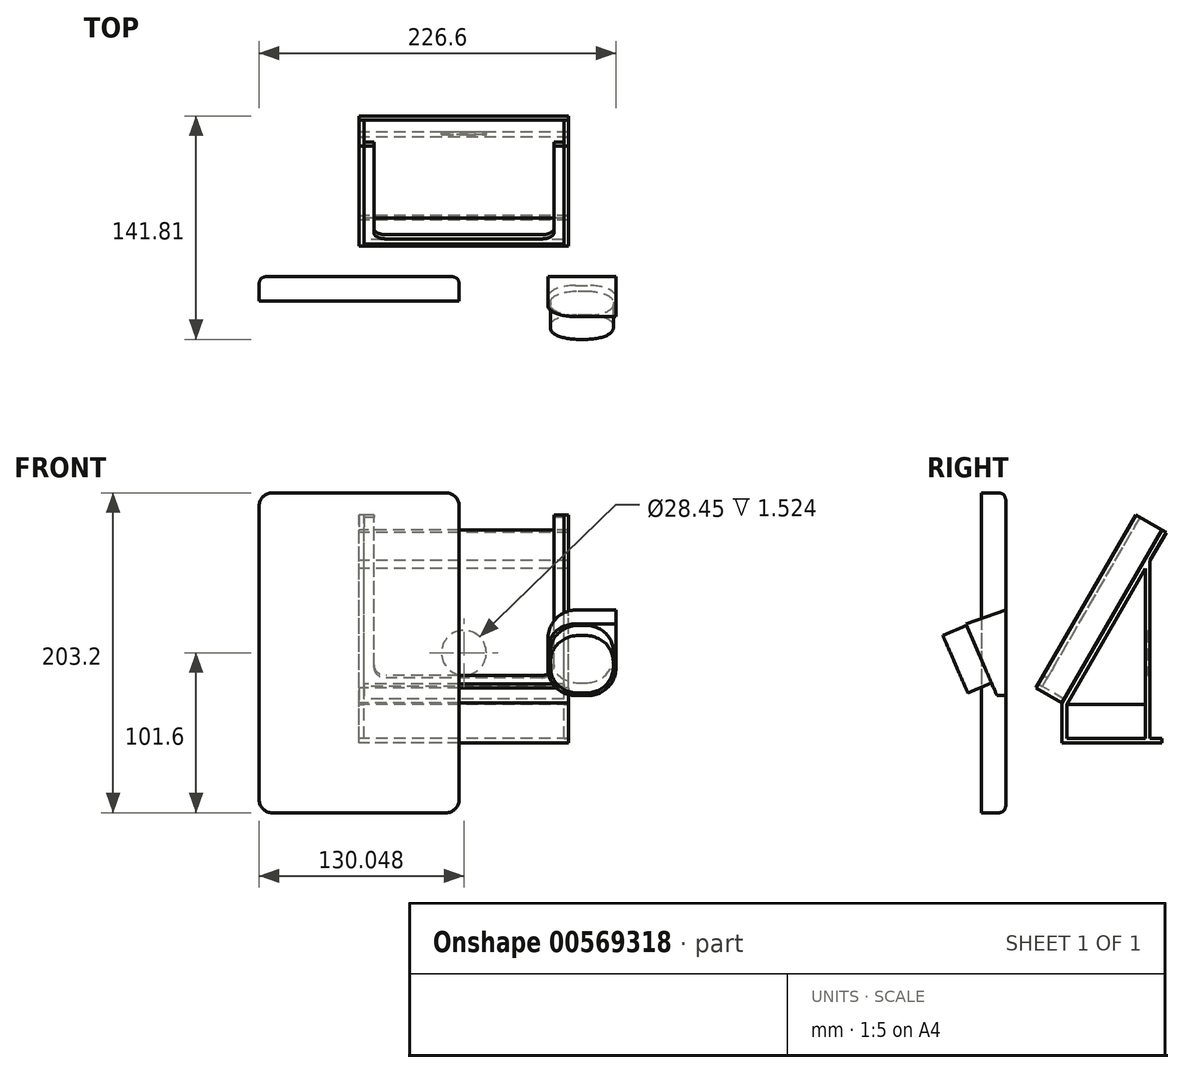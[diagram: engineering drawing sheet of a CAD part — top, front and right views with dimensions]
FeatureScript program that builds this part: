
annotation { "Feature Type Name" : "Feature", "Feature Type Description" : "" }
export const myFeature = defineFeature(function(context is Context, id is Id, definition is map)
    precondition{}
    {
        {
            var Q0;
            Q0=qCreatedBy(makeId("Front.planeOp"),FACE);
            var sketch = newSketch(context, id + "F0", { "sketchPlane" : qUnion([Q0])});
            skLineSegment(sketch, "E0.bottom", {"start": v(63.5, 101.6) * mm, "end": v(-63.5, 101.6) * mm});
            skLineSegment(sketch, "E0.top", {"start": v(63.5, -101.6) * mm, "end": v(-63.5, -101.6) * mm});
            skLineSegment(sketch, "E0.left", {"start": v(63.5, 101.6) * mm, "end": v(63.5, -101.6) * mm});
            skLineSegment(sketch, "E0.right", {"start": v(-63.5, 101.6) * mm, "end": v(-63.5, -101.6) * mm});
            skPoint(sketch, "E0.middle", {"position": v(0, 0) * mm});
            skSolve(sketch);
        }
        {
            var Q0;
            Q0=makeQuery(id+"F0.imprint","IMPRINT",FACE,{"disambiguationData":[TD([[makeQuery(id+"F0.imprint","IMPRINT",EDGE,{"derivedFrom":sQuery(id+"F0.wireOp",EDGE,"E0.bottom")}),1.0]])]});
            extrude(context, id + "F1", {"entities" : qUnion([Q0]), "depth" : 15.44 * mm, "offsetDistance" : 25.4 * mm});
        }
        {
            var Q0;
            Q0=makeQuery(id+"F1.opExtrude","SWEPT_EDGE",EDGE,{"disambiguationData":[OSD([sQuery(id+"F0.wireOp",EDGE,"E0.top"),sQuery(id+"F0.wireOp",EDGE,"E0.right")])]});
            var Q1;
            Q1=makeQuery(id+"F1.opExtrude","SWEPT_EDGE",EDGE,{"disambiguationData":[OSD([sQuery(id+"F0.wireOp",EDGE,"E0.top"),sQuery(id+"F0.wireOp",EDGE,"E0.left")])]});
            var Q2;
            Q2=makeQuery(id+"F1.opExtrude","SWEPT_EDGE",EDGE,{"disambiguationData":[OSD([sQuery(id+"F0.wireOp",EDGE,"E0.bottom"),sQuery(id+"F0.wireOp",EDGE,"E0.left")])]});
            var Q3;
            Q3=makeQuery(id+"F1.opExtrude","SWEPT_EDGE",EDGE,{"disambiguationData":[OSD([sQuery(id+"F0.wireOp",EDGE,"E0.bottom"),sQuery(id+"F0.wireOp",EDGE,"E0.right")])]});
            fillet(context, id + "F2", {"entities" : qUnion([Q0, Q1, Q2, Q3]), "radius" : 8.38 * mm, "tangentPropagation" : true, "allowEdgeOverflow" : false});
        }
        {
            var Q0;
            Q0=makeQuery(id+"F1.opExtrude","CAP_FACE",FACE,{"disambiguationData":[OSD([sQuery(id+"F0.wireOp",EDGE,"E0.bottom"),sQuery(id+"F0.wireOp",EDGE,"E0.top"),sQuery(id+"F0.wireOp",EDGE,"E0.left"),sQuery(id+"F0.wireOp",EDGE,"E0.right")])],"isStart":true});
            fillet(context, id + "F3", {"entities" : qUnion([Q0]), "radius" : 5.08 * mm, "tangentPropagation" : true, "rho" : .5, "crossSection" : FilletCrossSection.CONIC, "allowEdgeOverflow" : false});
        }
        {
            var Q0;
            Q0=qCreatedBy(makeId("Front.planeOp"),FACE);
            var sketch = newSketch(context, id + "F4", { "sketchPlane" : qUnion([Q0])});
            skLineSegment(sketch, "E1.bottom", {"start": v(163.1, 27.18) * mm, "end": v(119.92, 27.18) * mm});
            skLineSegment(sketch, "E1.top", {"start": v(163.1, -27.18) * mm, "end": v(119.92, -27.18) * mm});
            skLineSegment(sketch, "E1.left", {"start": v(163.1, 27.18) * mm, "end": v(163.1, -27.18) * mm});
            skLineSegment(sketch, "E1.right", {"start": v(119.92, 27.18) * mm, "end": v(119.92, -27.18) * mm});
            skPoint(sketch, "E1.middle", {"position": v(141.51, 0) * mm});
            skPoint(sketch, "E2.visualSharp", {"position": v(119.92, 27.18) * mm});
            skPoint(sketch, "E3.visualSharp", {"position": v(163.1, 27.18) * mm});
            skPoint(sketch, "E4.visualSharp", {"position": v(119.92, -27.18) * mm});
            skPoint(sketch, "E5.visualSharp", {"position": v(163.1, -27.18) * mm});
            skSolve(sketch);
        }
        {
            var Q0;
            Q0=makeQuery(id+"F4.imprint","IMPRINT",FACE,{"disambiguationData":[TD([[makeQuery(id+"F4.imprint","IMPRINT",EDGE,{"derivedFrom":sQuery(id+"F4.wireOp",EDGE,"E1.bottom")}),1.0]])]});
            extrude(context, id + "F5", {"entities" : qUnion([Q0]), "depth" : 25.4 * mm, "offsetDistance" : 25.4 * mm});
        }
        {
            var Q0;
            Q0=makeQuery(id+"F5.opExtrude","SWEPT_FACE",FACE,{"disambiguationData":[OSD([sQuery(id+"F4.wireOp",EDGE,"E1.left")])]});
            var sketch = newSketch(context, id + "F6", { "sketchPlane" : qUnion([Q0])});
            skLineSegment(sketch, "E6.0", {"start": v(-25.4, 27.18) * mm, "end": v(0, 27.18) * mm});
            skLineSegment(sketch, "E7", {"start": v(-5.56, -27.18) * mm, "end": v(-25.4, 18.47) * mm});
            skLineSegment(sketch, "E8", {"start": v(0, 27.18) * mm, "end": v(-25.4, 18.47) * mm});
            skLineSegment(sketch, "E9", {"start": v(-5.56, -27.18) * mm, "end": v(-25.4, -27.18) * mm});
            skLineSegment(sketch, "E10", {"start": v(-25.4, -27.18) * mm, "end": v(-25.4, 18.47) * mm});
            skLineSegment(sketch, "E11", {"start": v(-25.4, 18.47) * mm, "end": v(-25.4, 27.18) * mm});
            skSolve(sketch);
        }
        {
            var Q0;
            {var subQ0=sQuery(id+"F6.wireOp",EDGE,"E9");Q0=makeQuery(id+"F6.imprint","IMPRINT",FACE,{"disambiguationData":[TD([[makeQuery(id+"F6.imprint","IMPRINT",EDGE,{"derivedFrom":subQ0}),-1.0]])]});}
            var Q1;
            {var subQ0=sQuery(id+"F6.wireOp",EDGE,"E7");var subQ1=sQuery(id+"F4.wireOp",EDGE,"E1.left");var subQ2=makeQuery(id+"F5.opExtrude","SWEPT_EDGE",EDGE,{"disambiguationData":[OSD([subQ1,sQuery(id+"F4.wireOp",EDGE,"E5.filletArc")])]});var subQ3=makeQuery(id+"F6.imprint","INTERSECT",VERTEX,{"derivedFrom":[subQ2,subQ0]});Q1=makeQuery(id+"F6.imprint","IMPRINT",FACE,{"disambiguationData":[TD([[makeQuery(id+"F6.imprint","IMPRINT",EDGE,{"disambiguationData":[TD([[subQ3,-1.0]])],"derivedFrom":subQ0}),1.0]])]});}
            var Q2;
            {var subQ1=sQuery(id+"F6.wireOp",EDGE,"E7");var subQ3=makeQuery(id+"F5.opExtrude","SWEPT_EDGE",EDGE,{"disambiguationData":[OSD([sQuery(id+"F4.wireOp",EDGE,"E1.left"),sQuery(id+"F4.wireOp",EDGE,"E3.filletArc")])]});var subQ4=makeQuery(id+"F6.imprint","INTERSECT",VERTEX,{"derivedFrom":[subQ3,subQ1]});Q2=makeQuery(id+"F6.imprint","IMPRINT",FACE,{"disambiguationData":[TD([[makeQuery(id+"F6.imprint","IMPRINT",EDGE,{"disambiguationData":[TD([[subQ4,-1.0]])],"derivedFrom":subQ1}),1.0]])]});}
            var Q3;
            Q3=makeQuery(id+"F6.imprint","IMPRINT",FACE,{"disambiguationData":[TD([[makeQuery(id+"F6.imprint","IMPRINT",EDGE,{"derivedFrom":sQuery(id+"F6.wireOp",EDGE,"E6.0")}),-1.0]])]});
            extrude(context, id + "F7", {"entities" : qUnion([Q0, Q1, Q2, Q3]), "operationType" : NewBodyOperationType.REMOVE, "oppositeDirection" : true, "depth" : 50.8 * mm, "offsetDistance" : 25.4 * mm});
        }
        {
            var Q0;
            Q0=makeQuery(id+"F5.opExtrude","SWEPT_EDGE",EDGE,{"disambiguationData":[OSD([sQuery(id+"F4.wireOp",EDGE,"E1.top"),sQuery(id+"F4.wireOp",EDGE,"E1.left")])]});
            var Q1;
            Q1=makeQuery(id+"F5.opExtrude","SWEPT_EDGE",EDGE,{"disambiguationData":[OSD([sQuery(id+"F4.wireOp",EDGE,"E1.top"),sQuery(id+"F4.wireOp",EDGE,"E1.right")])]});
            var Q2;
            Q2=makeQuery(id+"F7.boolean.opBoolean","INTERSECT",EDGE,{"derivedFrom":[makeQuery(id+"F5.opExtrude","SWEPT_FACE",FACE,{"disambiguationData":[OSD([sQuery(id+"F4.wireOp",EDGE,"E1.right")])]}),makeQuery(id+"F7.opExtrude","SWEPT_FACE",FACE,{"disambiguationData":[OSD([sQuery(id+"F6.wireOp",EDGE,"E8")])]})]});
            var Q3;
            Q3=makeQuery(id+"F7.boolean.opBoolean","COPY",EDGE,{"derivedFrom":makeQuery(id+"F7.opExtrude","CAP_EDGE",EDGE,{"disambiguationData":[OSD([sQuery(id+"F6.wireOp",EDGE,"E8")])],"isStart":true})});
            fillet(context, id + "F8", {"entities" : qUnion([Q0, Q1, Q2, Q3]), "radius" : 17.53 * mm, "tangentPropagation" : true, "allowEdgeOverflow" : false});
        }
        {
            var Q0;
            Q0=makeQuery(id+"F7.boolean.opBoolean","COPY",FACE,{"derivedFrom":makeQuery(id+"F7.opExtrude","SWEPT_FACE",FACE,{"disambiguationData":[OSD([sQuery(id+"F6.wireOp",EDGE,"E7")])]})});
            var sketch = newSketch(context, id + "F9", { "sketchPlane" : qUnion([Q0])});
            skLineSegment(sketch, "E12.0", {"start": v(121.6, 25.92) * mm, "end": v(161.41, 25.92) * mm});
            skLineSegment(sketch, "E13.0", {"start": v(121.6, -13.88) * mm, "end": v(161.41, -13.88) * mm});
            skLineSegment(sketch, "E14.0", {"start": v(161.41, -13.88) * mm, "end": v(161.41, 25.92) * mm});
            skLineSegment(sketch, "E15.0", {"start": v(121.6, -13.88) * mm, "end": v(121.6, 25.92) * mm});
            skPoint(sketch, "E16.orphan", {"position": v(137.45, 25.92) * mm});
            skPoint(sketch, "E17.orphan", {"position": v(145.57, 25.92) * mm});
            skPoint(sketch, "E18.orphan", {"position": v(137.45, -13.88) * mm});
            skPoint(sketch, "E19.orphan", {"position": v(145.57, -13.88) * mm});
            skSolve(sketch);
        }
        {
            var Q0;
            {var subQ1=makeQuery(id+"F7.boolean.opBoolean","COPY",FACE,{"derivedFrom":makeQuery(id+"F7.opExtrude","SWEPT_FACE",FACE,{"disambiguationData":[OSD([sQuery(id+"F6.wireOp",EDGE,"E7")])]})});var subQ6=sQuery(id+"F6.wireOp",EDGE,"E8");var subQ14=makeQuery(id+"F8.opFillet","BLEND_EDGE",EDGE,{"blendedFrom":[makeQuery(id+"F7.boolean.opBoolean","COPY",EDGE,{"derivedFrom":makeQuery(id+"F7.opExtrude","CAP_EDGE",EDGE,{"disambiguationData":[OSD([subQ6])],"isStart":true})}),subQ1],"blendedInto":[subQ1]});var subQ16=sQuery(id+"F9.wireOp",EDGE,"E12.0");var subQ17=makeQuery(id+"F9.imprint","INTERSECT",VERTEX,{"derivedFrom":[subQ14,subQ16]});Q0=makeQuery(id+"F9.imprint","IMPRINT",FACE,{"disambiguationData":[TD([[makeQuery(id+"F9.imprint","IMPRINT",EDGE,{"disambiguationData":[TD([[subQ17,1.0]])],"derivedFrom":subQ16}),-1.0]])]});}
            var Q1;
            {var subQ0=sQuery(id+"F9.wireOp",EDGE,"E15.0");var subQ1=sQuery(id+"F9.wireOp",EDGE,"E12.0");var subQ2=makeQuery(id+"F9.imprint","INTERSECT",VERTEX,{"derivedFrom":[subQ1,subQ0]});Q1=makeQuery(id+"F9.imprint","IMPRINT",FACE,{"disambiguationData":[TD([[makeQuery(id+"F9.imprint","IMPRINT",EDGE,{"disambiguationData":[TD([[subQ2,-1.0]])],"derivedFrom":subQ1}),-1.0]])]});}
            var Q2;
            {var subQ0=sQuery(id+"F9.wireOp",EDGE,"E15.0");var subQ1=sQuery(id+"F9.wireOp",EDGE,"E13.0");var subQ2=makeQuery(id+"F9.imprint","INTERSECT",VERTEX,{"derivedFrom":[subQ1,subQ0]});Q2=makeQuery(id+"F9.imprint","IMPRINT",FACE,{"disambiguationData":[TD([[makeQuery(id+"F9.imprint","IMPRINT",EDGE,{"disambiguationData":[TD([[subQ2,-1.0]])],"derivedFrom":subQ1}),1.0]])]});}
            var Q3;
            {var subQ0=sQuery(id+"F9.wireOp",EDGE,"E14.0");var subQ1=sQuery(id+"F9.wireOp",EDGE,"E13.0");var subQ2=makeQuery(id+"F9.imprint","INTERSECT",VERTEX,{"derivedFrom":[subQ1,subQ0]});Q3=makeQuery(id+"F9.imprint","IMPRINT",FACE,{"disambiguationData":[TD([[makeQuery(id+"F9.imprint","IMPRINT",EDGE,{"disambiguationData":[TD([[subQ2,1.0]])],"derivedFrom":subQ1}),1.0]])]});}
            var Q4;
            {var subQ0=sQuery(id+"F9.wireOp",EDGE,"E14.0");var subQ1=sQuery(id+"F9.wireOp",EDGE,"E12.0");var subQ2=makeQuery(id+"F9.imprint","INTERSECT",VERTEX,{"derivedFrom":[subQ1,subQ0]});Q4=makeQuery(id+"F9.imprint","IMPRINT",FACE,{"disambiguationData":[TD([[makeQuery(id+"F9.imprint","IMPRINT",EDGE,{"disambiguationData":[TD([[subQ2,1.0]])],"derivedFrom":subQ1}),-1.0]])]});}
            extrude(context, id + "F10", {"entities" : qUnion([Q0, Q1, Q2, Q3, Q4]), "depth" : 16.28 * mm, "offsetDistance" : 25.4 * mm});
        }
        {
            var Q0;
            Q0=makeQuery(id+"F10.opExtrude","SWEPT_EDGE",EDGE,{"disambiguationData":[OSD([sQuery(id+"F9.wireOp",EDGE,"E13.0"),sQuery(id+"F9.wireOp",EDGE,"E14.0")])]});
            var Q1;
            Q1=makeQuery(id+"F10.opExtrude","SWEPT_EDGE",EDGE,{"disambiguationData":[OSD([sQuery(id+"F9.wireOp",EDGE,"E12.0"),sQuery(id+"F9.wireOp",EDGE,"E14.0")])]});
            var Q2;
            Q2=makeQuery(id+"F10.opExtrude","SWEPT_EDGE",EDGE,{"disambiguationData":[OSD([sQuery(id+"F9.wireOp",EDGE,"E13.0"),sQuery(id+"F9.wireOp",EDGE,"E15.0")])]});
            var Q3;
            Q3=makeQuery(id+"F10.opExtrude","SWEPT_EDGE",EDGE,{"disambiguationData":[OSD([sQuery(id+"F9.wireOp",EDGE,"E12.0"),sQuery(id+"F9.wireOp",EDGE,"E15.0")])]});
            fillet(context, id + "F11", {"entities" : qUnion([Q0, Q1, Q2, Q3]), "radius" : 17.53 * mm, "tangentPropagation" : true, "allowEdgeOverflow" : false});
        }
        {
            var Q0;
            Q0=qCreatedBy(makeId("Right.planeOp"),FACE);
            var sketch = newSketch(context, id + "F12", { "sketchPlane" : qUnion([Q0])});
            skLineSegment(sketch, "E20", {"start": v(99.29, -57.37) * mm, "end": v(35.79, -57.37) * mm});
            skLineSegment(sketch, "E21", {"start": v(35.79, -57.37) * mm, "end": v(35.79, -31.97) * mm});
            skLineSegment(sketch, "E22", {"start": v(35.79, -31.97) * mm, "end": v(99.29, 78.02) * mm});
            skLineSegment(sketch, "E23.0", {"start": v(38.84, -32.78) * mm, "end": v(88.62, 53.44) * mm});
            skLineSegment(sketch, "E23.1", {"start": v(38.84, -54.32) * mm, "end": v(38.84, -32.78) * mm});
            skLineSegment(sketch, "E23.2", {"start": v(99.29, -54.32) * mm, "end": v(91.67, -54.32) * mm});
            skLineSegment(sketch, "E24", {"start": v(99.29, 78.02) * mm, "end": v(101.93, 76.5) * mm});
            skLineSegment(sketch, "E25", {"start": v(99.29, -57.37) * mm, "end": v(99.29, -54.32) * mm});
            skLineSegment(sketch, "E26", {"start": v(91.67, -54.32) * mm, "end": v(91.67, 58.72) * mm});
            skLineSegment(sketch, "E27.0", {"start": v(88.62, -54.32) * mm, "end": v(88.62, 53.44) * mm});
            skLineSegment(sketch, "E28.trimOffspring", {"start": v(91.67, 58.72) * mm, "end": v(101.93, 76.5) * mm});
            skLineSegment(sketch, "E29.trimOffspring", {"start": v(88.62, -54.32) * mm, "end": v(38.84, -54.32) * mm});
            skSolve(sketch);
        }
        {
            var Q0;
            Q0=makeQuery(id+"F12.imprint","IMPRINT",FACE,{"disambiguationData":[TD([[makeQuery(id+"F12.imprint","IMPRINT",EDGE,{"derivedFrom":sQuery(id+"F12.wireOp",EDGE,"E20")}),-1.0]])]});
            extrude(context, id + "F13", {"entities" : qUnion([Q0]), "depth" : 133.1 * mm, "offsetDistance" : 25.4 * mm});
        }
        {
            var Q0;
            Q0=makeQuery(id+"F13.opExtrude","SWEPT_FACE",FACE,{"disambiguationData":[OSD([sQuery(id+"F12.wireOp",EDGE,"E22")])]});
            var sketch = newSketch(context, id + "F14", { "sketchPlane" : qUnion([Q0])});
            skLineSegment(sketch, "E30.0", {"start": v(0, -9.8) * mm, "end": v(0, 117.2) * mm});
            skLineSegment(sketch, "E30.1", {"start": v(133.1, -9.8) * mm, "end": v(133.1, 117.2) * mm});
            skLineSegment(sketch, "E30.2", {"start": v(133.1, -9.8) * mm, "end": v(0, -9.8) * mm});
            skLineSegment(sketch, "E31.0", {"start": v(3.05, -6.74) * mm, "end": v(3.05, 193.4) * mm});
            skLineSegment(sketch, "E31.1", {"start": v(130.05, -6.74) * mm, "end": v(3.05, -6.74) * mm});
            skLineSegment(sketch, "E31.2", {"start": v(130.05, -6.74) * mm, "end": v(130.05, 117.2) * mm});
            skLineSegment(sketch, "E32", {"start": v(123.7, 117.2) * mm, "end": v(133.1, 117.2) * mm});
            skLineSegment(sketch, "E33.0", {"start": v(9.4, 7.23) * mm, "end": v(9.4, 193.4) * mm});
            skLineSegment(sketch, "E34.0", {"start": v(116.08, -0.4) * mm, "end": v(17.02, -0.4) * mm});
            skLineSegment(sketch, "E35.0", {"start": v(123.7, 7.23) * mm, "end": v(123.7, 117.2) * mm});
            skArc(sketch, "E36.filletArc", {"start": v(9.4, 7.23) * mm, "mid": v(11.63, 1.84) * mm, "end": v(17.02, -0.4) * mm});
            skArc(sketch, "E37.filletArc", {"start": v(116.08, -0.4) * mm, "mid": v(121.47, 1.84) * mm, "end": v(123.7, 7.23) * mm});
            skSolve(sketch);
        }
        {
            var Q0;
            {var subQ1=sQuery(id+"F14.wireOp",EDGE,"E30.0");Q0=makeQuery(id+"F14.imprint","IMPRINT",FACE,{"disambiguationData":[TD([[makeQuery(id+"F14.imprint","IMPRINT",EDGE,{"derivedFrom":subQ1}),-1.0]])]});}
            extrude(context, id + "F15", {"entities" : qUnion([Q0]), "depth" : 19.05 * mm, "offsetDistance" : 25.4 * mm});
        }
        {
            var Q0;
            {var subQ4=sQuery(id+"F14.wireOp",EDGE,"E31.0");Q0=makeQuery(id+"F14.imprint","IMPRINT",FACE,{"disambiguationData":[TD([[makeQuery(id+"F14.imprint","IMPRINT",EDGE,{"derivedFrom":subQ4}),-1.0]])]});}
            extrude(context, id + "F16", {"entities" : qUnion([Q0]), "depth" : 19.05 * mm, "offsetDistance" : 25.4 * mm, "hasSecondDirection" : true, "secondDirectionOppositeDirection" : true, "secondDirectionDepth" : -16 * mm});
        }
        {
            var Q0;
            Q0=makeQuery(id+"F13.opExtrude","CAP_FACE",FACE,{"disambiguationData":[OSD([sQuery(id+"F12.wireOp",EDGE,"E20"),sQuery(id+"F12.wireOp",EDGE,"E21"),sQuery(id+"F12.wireOp",EDGE,"E22"),sQuery(id+"F12.wireOp",EDGE,"E23.0"),sQuery(id+"F12.wireOp",EDGE,"E23.1"),sQuery(id+"F12.wireOp",EDGE,"E23.2"),sQuery(id+"F12.wireOp",EDGE,"E24"),sQuery(id+"F12.wireOp",EDGE,"E25"),sQuery(id+"F12.wireOp",EDGE,"E26"),sQuery(id+"F12.wireOp",EDGE,"E27.0"),sQuery(id+"F12.wireOp",EDGE,"E28.trimOffspring"),sQuery(id+"F12.wireOp",EDGE,"E29.trimOffspring")])],"isStart":false});
            var sketch = newSketch(context, id + "F17", { "sketchPlane" : qUnion([Q0])});
            skLineSegment(sketch, "E38.0", {"start": v(38.84, -54.32) * mm, "end": v(38.84, -32.78) * mm});
            skLineSegment(sketch, "E39.0", {"start": v(88.62, -54.32) * mm, "end": v(38.84, -54.32) * mm});
            skLineSegment(sketch, "E40", {"start": v(38.84, -32.78) * mm, "end": v(88.62, -32.78) * mm});
            skLineSegment(sketch, "E41", {"start": v(88.62, -32.78) * mm, "end": v(88.62, -54.32) * mm});
            skSolve(sketch);
        }
        {
            var Q0;
            Q0=makeQuery(id+"F17.imprint","IMPRINT",FACE,{"disambiguationData":[TD([[makeQuery(id+"F17.imprint","IMPRINT",EDGE,{"derivedFrom":sQuery(id+"F17.wireOp",EDGE,"E38.0")}),-1.0]])]});
            extrude(context, id + "F18", {"entities" : qUnion([Q0]), "oppositeDirection" : true, "depth" : 3.05 * mm, "offsetDistance" : 25.4 * mm});
        }
        {
            var Q0;
            Q0=makeQuery(id+"F18.opExtrude","CAP_FACE",FACE,{"disambiguationData":[OSD([sQuery(id+"F17.wireOp",EDGE,"E38.0"),sQuery(id+"F17.wireOp",EDGE,"E39.0"),sQuery(id+"F17.wireOp",EDGE,"E40"),sQuery(id+"F17.wireOp",EDGE,"E41")])],"isStart":false});
            var Q1;
            Q1=makeQuery(id+"F13.opExtrude","CAP_FACE",FACE,{"disambiguationData":[OSD([sQuery(id+"F12.wireOp",EDGE,"E20"),sQuery(id+"F12.wireOp",EDGE,"E21"),sQuery(id+"F12.wireOp",EDGE,"E22"),sQuery(id+"F12.wireOp",EDGE,"E23.0"),sQuery(id+"F12.wireOp",EDGE,"E23.1"),sQuery(id+"F12.wireOp",EDGE,"E23.2"),sQuery(id+"F12.wireOp",EDGE,"E24"),sQuery(id+"F12.wireOp",EDGE,"E25"),sQuery(id+"F12.wireOp",EDGE,"E26"),sQuery(id+"F12.wireOp",EDGE,"E27.0"),sQuery(id+"F12.wireOp",EDGE,"E28.trimOffspring"),sQuery(id+"F12.wireOp",EDGE,"E29.trimOffspring")])],"isStart":true});
            extrude(context, id + "F19", {"entities" : qUnion([Q0]), "operationType" : NewBodyOperationType.ADD, "endBound" : BoundingType.UP_TO_SURFACE, "depth" : 127 * mm, "endBoundEntityFace" : qUnion([Q1]), "offsetDistance" : 25.4 * mm, "hasSecondDirection" : true, "secondDirectionOppositeDirection" : true, "secondDirectionDepth" : -127 * mm});
        }
        {
            var Q0;
            Q0=makeQuery(id+"F13.opExtrude","SWEPT_FACE",FACE,{"disambiguationData":[OSD([sQuery(id+"F12.wireOp",EDGE,"E26")])]});
            var sketch = newSketch(context, id + "F20", { "sketchPlane" : qUnion([Q0])});
            skCircle(sketch, "E42", {"center": v(-66.55, 0) * mm, "radius": 14.22 * mm});
            skSolve(sketch);
        }
        {
            var Q0;
            Q0=makeQuery(id+"F20.imprint","IMPRINT",FACE,{"disambiguationData":[TD([[makeQuery(id+"F20.imprint","IMPRINT",EDGE,{"derivedFrom":sQuery(id+"F20.wireOp",EDGE,"E42")}),1.0]])]});
            extrude(context, id + "F21", {"entities" : qUnion([Q0]), "operationType" : NewBodyOperationType.REMOVE, "oppositeDirection" : true, "depth" : 1.52 * mm, "offsetDistance" : 25.4 * mm});
        }
    });
